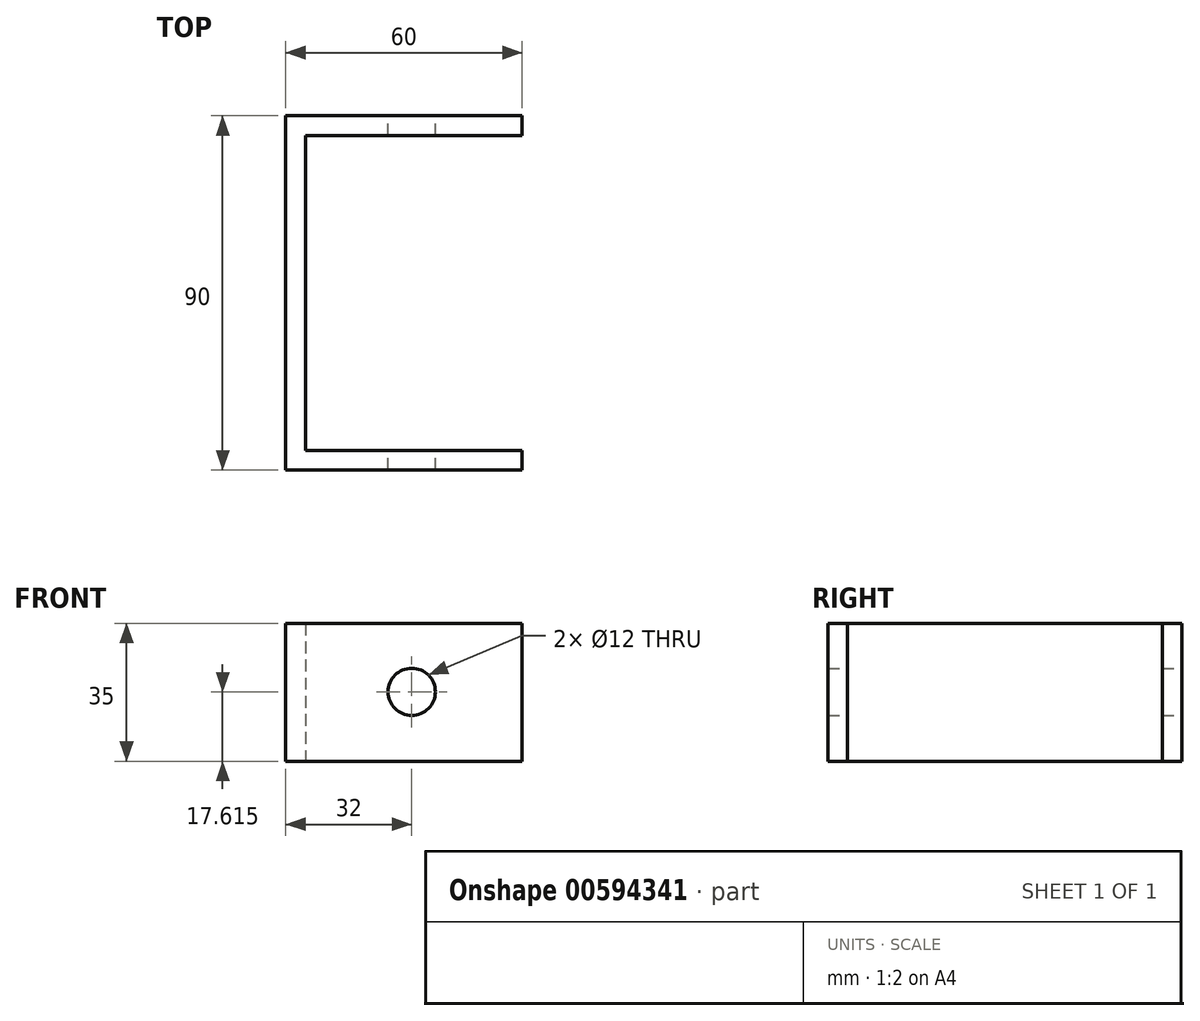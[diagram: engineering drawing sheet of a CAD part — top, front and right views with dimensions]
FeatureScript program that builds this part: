
annotation { "Feature Type Name" : "Feature", "Feature Type Description" : "" }
export const myFeature = defineFeature(function(context is Context, id is Id, definition is map)
    precondition{}
    {
        {
            var Q0;
            Q0=qCreatedBy(makeId("Top.planeOp"),FACE);
            var sketch = newSketch(context, id + "F0", { "sketchPlane" : qUnion([Q0])});
            skLineSegment(sketch, "E0.bottom", {"start": v(0, 0) * mm, "end": v(-5, 0) * mm});
            skLineSegment(sketch, "E0.top", {"start": v(0, 45) * mm, "end": v(-5, 45) * mm});
            skLineSegment(sketch, "E0.left", {"start": v(0, 0) * mm, "end": v(0, 45) * mm});
            skLineSegment(sketch, "E0.right", {"start": v(-5, 0) * mm, "end": v(-5, 45) * mm});
            skPoint(sketch, "E1.oppositeSnap0", {"position": v(-2.5, 45) * mm});
            skLineSegment(sketch, "E1.bottom", {"start": v(0, 40) * mm, "end": v(55, 40) * mm});
            skLineSegment(sketch, "E1.top", {"start": v(0, 45) * mm, "end": v(55, 45) * mm});
            skLineSegment(sketch, "E1.left", {"start": v(0, 40) * mm, "end": v(0, 45) * mm});
            skLineSegment(sketch, "E1.right", {"start": v(55, 40) * mm, "end": v(55, 45) * mm});
            skLineSegment(sketch, "E2.MirrorCS", {"start": v(-5, 0) * mm, "end": v(-5, -45) * mm});
            skLineSegment(sketch, "E3.MirrorCS", {"start": v(0, 0) * mm, "end": v(0, -45) * mm});
            skLineSegment(sketch, "E4.MirrorCS", {"start": v(0, -45) * mm, "end": v(-5, -45) * mm});
            skLineSegment(sketch, "E5.MirrorCS", {"start": v(0, -45) * mm, "end": v(55, -45) * mm});
            skLineSegment(sketch, "E6.MirrorCS", {"start": v(0, -40) * mm, "end": v(55, -40) * mm});
            skLineSegment(sketch, "E7.MirrorCS", {"start": v(55, -40) * mm, "end": v(55, -45) * mm});
            skSolve(sketch);
        }
        {
            var Q0;
            Q0 = qSketchRegion(id + "F0", true);
            extrude(context, id + "F1", {"entities" : qUnion([Q0]), "depth" : 35 * mm, "offsetDistance" : 25.4 * mm});
        }
        {
            var Q0;
            Q0=makeQuery(id+"F1.opExtrude","SWEPT_FACE",FACE,{"disambiguationData":[OSD([sQuery(id+"F0.wireOp",EDGE,"E0.top"),sQuery(id+"F0.wireOp",EDGE,"E1.top")])]});
            var sketch = newSketch(context, id + "F2", { "sketchPlane" : qUnion([Q0])});
            skCircle(sketch, "E8", {"center": v(-27, 17.61) * mm, "radius": 6 * mm});
            skSolve(sketch);
        }
        {
            var Q0;
            Q0=sQuery(id+"F2.wireOp",VERTEX,"E8.center");
            var Q1;
            Q1=makeQuery(id+"F1.opExtrude","SWEPT_BODY",BODY,{"disambiguationData":[OSD([sQuery(id+"F0.wireOp",EDGE,"E0.top"),sQuery(id+"F0.wireOp",EDGE,"E0.left"),sQuery(id+"F0.wireOp",EDGE,"E0.right"),sQuery(id+"F0.wireOp",EDGE,"E1.bottom"),sQuery(id+"F0.wireOp",EDGE,"E1.top"),sQuery(id+"F0.wireOp",EDGE,"E1.right"),sQuery(id+"F0.wireOp",EDGE,"E2.MirrorCS"),sQuery(id+"F0.wireOp",EDGE,"E3.MirrorCS"),sQuery(id+"F0.wireOp",EDGE,"E4.MirrorCS"),sQuery(id+"F0.wireOp",EDGE,"E5.MirrorCS"),sQuery(id+"F0.wireOp",EDGE,"E6.MirrorCS"),sQuery(id+"F0.wireOp",EDGE,"E7.MirrorCS")])]});
            hole(context, id + "F3", {"style" : HoleStyle.SIMPLE, "endStyle" : HoleEndStyle.THROUGH, "holeDiameter" : 12 * mm, "majorDiameter" : 6.35 * mm, "isTappedThrough" : true, "tappedDepth" : 12.7 * mm, "tapClearance" : 3, "locations" : qUnion([Q0]), "scope" : qUnion([Q1])});
        }
    });
